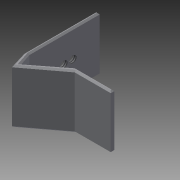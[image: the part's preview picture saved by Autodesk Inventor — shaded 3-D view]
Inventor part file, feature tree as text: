
AUTODESK INVENTOR PART (.ipt)
format: ipt  version: 2015 (Build 190159000, 159)  size: 120,320 bytes
history: native  units: in
note: dims shown in document units (in); Inventor stores cm internally (conversion verified against a paired STEP export)
features: sketch x2, extrude x1, hole x1, chamfer x1
ambient origin geometry x8: Origin, YZ Plane, XZ Plane, XY Plane, X Axis, Y Axis, Z Axis, Center Point
bodies: Solid1 (feature_tree)
feature tree (5):
  extrude  "Extrusion1"  Depth=1.0in
  hole  "Hole1"  [1 undecoded]
  chamfer  "Chamfer1"  Distance=0.481in
  sketch  "Sketch1"  dims[d0=0.75in d1=1.0in]
  sketch  "Sketch2"  dims[d2=2.0in d3=0.481in d4=0.481in d5=0.1in d6=0.1in d7=1.0in d8=1.5in d9=0.0in d10=0.75in d11=0.25in d12=0.75in d13=0.196in d14=0.5in d15=0.375in d16=0.25in d17=0.5635in d18=1.0in d19=0.8108in d20=0.04in d21=0.125in d22=45.0deg]
note: 1 required parameter value undecoded (feature->parameter linkage not recoverable at this tier; creation-order binding heuristic only, values carry confidence <= 0.55)
